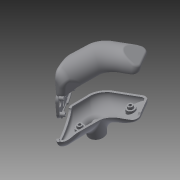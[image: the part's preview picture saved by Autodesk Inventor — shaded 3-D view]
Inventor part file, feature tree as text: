
AUTODESK INVENTOR PART (.ipt)
format: ipt  version: 2014 SP1 (Build 180222100, 222)  size: 21,332,480 bytes
history: native  units: in
note: dims shown in document units (in); Inventor stores cm internally (conversion verified against a paired STEP export)
features: sketch x38, surface_op x32, other x30, extrude x28, fillet x22, draft x19, chamfer x18, plane x14, projected_geometry x6, shell x4, move_body x3, loft x2, delete_face x1, boolean_combine x1, split x1
ambient origin geometry x8: Origin, YZ Plane, XZ Plane, XY Plane, X Axis, Y Axis, Z Axis, Center Point
bodies: Solid1 (feature_tree), Solid2 (feature_tree), Solid5 (feature_tree), Solid8 (feature_tree), Solid9 (feature_tree), Solid10 (feature_tree), Solid6 (feature_tree), Solid7 (feature_tree)
feature tree (219):
  sketch  "Sketch1"  dims[d0=0.7in d1=0.6in]
  plane  "Work Plane1"
  sketch  "Sketch2"  dims[d2=2.0in d3=0.73in]
  loft  "Loft1"
  plane  "Work Plane3"
  plane  "Work Plane4"
  plane  "Work Plane6"
  delete_face  "Delete Face1"
  surface_op  "Extend1"
  sketch  "Sketch6"  dims[d4=0.68in d5=120.0deg d6=0.8125in d9=0.75in]
  surface_op  "Stitch Surface1"
  extrude  "Extrusion5"  Depth=2.0in
  extrude  "Extrusion6"  Depth=0.8125in TaperAngle=120.0deg
  boolean_combine  "Combine1"
  extrude  "Extrusion7"  TaperAngle=0.0deg  [1 undecoded]
  loft  "Loft5"
  fillet  "Fillet6"  Radius=1.0in
  fillet  "Fillet7"  Radius=0.1969in
  plane  "Work Plane7"
  plane  "Work Plane8"
  extrude  "Extrusion10"  Depth=0.1969in
  draft  "FaceDraft1"
  fillet  "Fillet15"  [1 undecoded]
  extrude  "Extrusion15"  TaperAngle=90.0deg  [1 undecoded]
  fillet  "Fillet19"  Radius=0.35in
  fillet  "Fillet20"  [1 undecoded]
  extrude  "Extrusion9"  Depth=0.1in
  fillet  "Fillet11"  Radius=0.0687in
  fillet  "Fillet22"  Radius=0.75in
  shell  "Shell1"  Thickness=0.875in
  extrude  "Extrusion16"  Depth=0.3937in
  extrude  "Extrusion11"  Depth=0.141in
  draft  "FaceDraft5"
  sketch  "3D Sketch2"
  plane  "Work Plane9"
  extrude  "Extrusion17"  Depth=0.3125in TaperAngle=0.0deg
  plane  "Work Plane10"
  extrude  "Extrusion18"  Depth=0.0172in
  plane  "Work Plane11"
  extrude  "Extrusion19"  Depth=0.225in
  plane  "Work Plane12"
  extrude  "Extrusion20"  Depth=0.13in
  draft  "FaceDraft2"
  draft  "FaceDraft3"
  extrude  "Extrusion21"  Depth=0.4in
  extrude  "Extrusion22"  [1 undecoded]
  sketch  "Sketch25"  dims[d130=-0.625in d131=0.4in]
  extrude  "Extrusion23"  Depth=1.0in TaperAngle=0.0deg
  extrude  "Extrusion24"  Depth=0.28in
  extrude  "Extrusion25"  [1 undecoded]
  draft  "FaceDraft4"
  extrude  "Extrusion26"  Depth=1.0in TaperAngle=0.0deg
  plane  "Work Plane13"
  sketch  "Sketch29"  dims[d140=1.0in d141=0.0in d142=-0.06in]
  plane  "Work Plane14"
  sketch  "Sketch30"  dims[d143=0.28in d144=1.0in d145=0.0in]
  surface_op  "Stitch Surface5"
  surface_op  "Extend3"
  surface_op  "Extend4"
  surface_op  "Stitch Surface6"
  sketch  "Sketch35"  dims[d151=0.13in d152=1.0in d153=0.0in]
  surface_op  "Stitch Surface7"
  split  "Split2"
  sketch  "Sketch39"  dims[d160=0.06in d161=1.0in d162=0.0in]
  extrude  "Extrusion27"  Depth=0.0206in
  chamfer  "Chamfer4"  Distance=1.0in
  chamfer  "Chamfer5"  Distance=1.0in
  chamfer  "Chamfer6"  Distance=1.0in
  chamfer  "Chamfer7"  Distance=1.0in
  chamfer  "Chamfer9"  Distance=1.0in
  chamfer  "Chamfer10"  Distance=1.0in
  chamfer  "Chamfer11"  [1 undecoded]
  chamfer  "Chamfer12"  [1 undecoded]
  chamfer  "Chamfer16"  Distance=0.1969in
  chamfer  "Chamfer17"  [1 undecoded]
  chamfer  "Chamfer18"  Distance=0.1969in
  chamfer  "Chamfer19"  [1 undecoded]
  chamfer  "Chamfer20"  [1 undecoded]
  chamfer  "Chamfer21"  [1 undecoded]
  chamfer  "Chamfer22"  [1 undecoded]
  chamfer  "Chamfer23"  [1 undecoded]
  chamfer  "Chamfer24"  [1 undecoded]
  chamfer  "Chamfer25"  [1 undecoded]
  extrude  "Extrusion29"  TaperAngle=0.0deg  [1 undecoded]
  draft  "FaceDraft6"
  fillet  "Fillet26"  [1 undecoded]
  move_body  "Move Body2"
  move_body  "Move Body3"
  draft  "FaceDraft7"
  draft  "FaceDraft8"
  draft  "FaceDraft9"
  draft  "FaceDraft10"
  extrude  "Extrusion30"  TaperAngle=0.0deg  [1 undecoded]
  draft  "FaceDraft16"
  draft  "FaceDraft17"
  extrude  "Extrusion31"  Depth=0.1969in
  extrude  "Extrusion32"  TaperAngle=0.0deg  [1 undecoded]
  extrude  "Extrusion33"  Depth=0.02in
  draft  "FaceDraft18"
  draft  "FaceDraft19"
  draft  "FaceDraft20"
  fillet  "Fillet28"  Radius=0.02in
  extrude  "Extrusion34"  TaperAngle=0.0deg  [1 undecoded]
  extrude  "Extrusion35"  Depth=0.1969in TaperAngle=0.0deg
  extrude  "Extrusion36"  TaperAngle=0.0deg  [1 undecoded]
  draft  "FaceDraft21"
  draft  "FaceDraft22"
  draft  "FaceDraft23"
  shell  "Shell2"  Thickness=0.1969in
  shell  "Shell3"  Thickness=0.1969in
  shell  "Shell4"  Thickness=0.0in
  fillet  "Fillet32"  Radius=0.1969in
  fillet  "Fillet29"  Radius=0.5in
  fillet  "Fillet30"  Radius=0.35in
  fillet  "Fillet31"  Radius=0.125in
  fillet  "Fillet33"  Radius=0.05in
  extrude  "Extrusion40"  Depth=0.05in TaperAngle=0.0deg
  draft  "FaceDraft26"
  fillet  "Fillet44"  Radius=0.05in
  fillet  "Fillet39"  Radius=0.05in
  move_body  "Move Body4"
  fillet  "Fillet45"  Radius=0.05in
  fillet  "Fillet46"  Radius=0.05in
  fillet  "Fillet37"  Radius=0.05in
  fillet  "Fillet48"  Radius=0.05in
  fillet  "Fillet49"  Radius=0.05in
  fillet  "Fillet50"  Radius=0.05in
  sketch  "Sketch57"  dims[d172=0.0in]
  sketch  "Sketch60"  dims[d173=0.1969in d174=0.0in d175=0.0in d176=0.1969in d177=0.0in d178=0.1969in d179=0.0in d184=0.0in d185=0.0in d187=0.0in d191=0.0in d192=0.0in d193=0.0in d197=0.0in d201=0.0in d204=0.0in d208=0.0in d209=0.1969in d210=0.0in d212=0.02in d213=0.02in d214=0.0in d216=0.1969in d217=0.1969in d218=0.0in d219=0.0in d220=0.1969in d221=0.1969in d222=0.0in d223=0.1969in d227=0.5in d228=0.35in d229=0.125in d233=0.05in d234=0.05in d235=0.0in d236=0.05in d237=0.125in d238=0.1374in d239=0.05in d240=0.125in d241=0.1374in d242=0.05in d243=0.125in d244=0.1374in d245=0.05in d246=0.125in d247=0.1374in d251=0.05in d252=0.125in d253=0.0687in d254=0.05in d255=0.125in d256=0.0687in d257=0.05in d258=0.125in d259=0.0687in d260=0.05in d261=0.125in d262=0.0687in d272=0.05in d273=0.125in d274=0.0687in d275=0.05in d276=0.125in d277=0.0687in d278=0.05in d279=0.125in d280=0.0687in d281=0.05in d282=0.125in d283=0.0687in d284=0.05in d285=0.125in d286=0.0687in d287=0.05in d288=0.125in d289=0.0687in d290=0.05in d291=0.125in d292=0.0687in d293=0.05in d294=0.125in d295=0.0687in d296=0.05in d297=0.125in d298=0.0687in d299=0.0508in d300=0.125in d301=0.0687in d302=0.05in d308=0.05in d309=0.0in d310=0.1374in d311=0.03in d312=0.0in d313=1.0in d314=0.0in d315=0.0in d316=-1.0in d317=0.0in d318=0.0206in d319=0.0206in d320=0.0206in d321=0.0206in d323=0.2756in d324=0.3in d325=0.025in d326=1.0in d327=0.0in d337=0.0206in d338=0.0206in d340=0.45in d341=0.08in d342=0.4in d344=0.52in d345=0.0962in d346=0.05in d347=0.025in d349=0.09in d350=0.0in d351=0.008in d352=0.09in d353=0.0in d354=0.008in d355=0.09in d356=0.0in d357=0.0206in d358=0.0206in d359=0.0206in d360=0.015in d361=0.01in d362=0.01in d363=0.01in d365=0.025in d366=0.04in d367=0.0in d371=0.04in d372=0.0in d373=0.04in d374=0.04in d375=0.0in d376=0.01in d377=0.04in d378=0.008in d379=0.04in d380=0.025in d381=0.0206in d382=0.0206in d383=0.0206in d384=0.04in d385=0.04in d386=0.01in d399=0.05in d400=0.075in d401=0.221in d402=0.0in d403=0.05in d404=0.075in d405=0.488in d406=0.04in d407=0.38in d409=-0.5in d410=0.0in d411=0.0in d412=0.01in d431=0.02in d437=0.01in d438=0.005in d439=0.005in d441=0.004in d442=0.003in d443=0.003in d444=0.2909in d445=0.0033in d446=0.6025in d447=0.1425in d448=0.1769in d449=0.5879in d450=1.0588in d451=0.0385in d452=0.2953in d453=1.2533in d454=1.2286in d455=0.3856in d456=0.075in d457=0.0069in d458=0.0143in]
  plane  "Work Plane2"
  plane  "Work Plane5"
  other  "Srf1"
  other  "Srf2"
  sketch  "Sketch8"  dims[d10=0.0in d11=90.0deg d12=0.0in d13=90.0deg]
  sketch  "Sketch9"  dims[d14=150.0deg d15=-0.5in d45=1.0in d46=0.0in d47=1.0in d48=0.0in d49=0.1969in]
  sketch  "Sketch11"  dims[d50=0.0in d51=0.1969in d52=0.0in]
  sketch  "Sketch12"  dims[d53=1.0in d54=0.0in d56=90.0deg d58=90.0deg]
  other  "Edges5"
  other  "Edges6"
  sketch  "Sketch13"  dims[d62=0.0in d63=90.0deg d64=0.0in d65=90.0deg d66=0.2875in d67=0.35in d78=90.0deg]
  sketch  "Sketch17"  dims[d79=1.0in d80=0.0in d81=0.1in d87=0.0687in d88=0.75in d89=0.875in d90=0.0in]
  sketch  "Sketch18"  dims[d92=0.3937in d93=0.3937in]
  projected_geometry  "Projected Loop3"
  other  "Silhouette Curve2"
  sketch  "Sketch19"  dims[d94=0.2625in d95=0.141in]
  sketch  "Sketch20"  dims[d96=0.5in d97=0.3125in d98=0.0in]
  sketch  "Sketch21"  dims[d107=0.1in d114=0.0172in]
  sketch  "Sketch22"  dims[d117=0.121in d118=0.0in]
  sketch  "Sketch23"  dims[d119=0.1in d120=0.1in d121=0.13in d122=0.1969in d123=0.3in d124=0.2169in d125=0.225in]
  sketch  "Sketch24"  dims[d126=0.15in d127=0.0in d129=0.13in]
  sketch  "Sketch26"  dims[d132=1.0in d133=0.0in d134=-0.875in]
  sketch  "Sketch27"  dims[d135=0.4in d136=1.0in d137=0.0in]
  sketch  "Sketch28"  dims[d138=-0.06in d139=0.28in]
  other  "Srf3"
  other  "Srf4"
  other  "Srf5"
  other  "Srf6"
  other  "Srf7"
  other  "Srf8"
  other  "Srf12"
  other  "Srf13"
  other  "Srf15"
  other  "Srf17"
  other  "Srf18"
  other  "Srf19"
  other  "Srf21"
  other  "Srf24"
  other  "Srf25"
  sketch  "Sketch33"  dims[d146=0.0206in d147=0.0206in]
  sketch  "Sketch34"  dims[d148=0.13in d149=1.0in d150=0.0in]
  other  "Srf28"
  other  "Srf30"
  other  "Srf31"
  other  "Srf32"
  other  "Srf33"
  other  "Srf34"
  other  "Srf35"
  sketch  "Sketch36"  dims[d154=0.06in]
  other  "Srf36"
  other  "Srf37"
  other  "Srf38"
  sketch  "Sketch37"  dims[d155=0.06in d156=1.0in d157=0.0in d158=1.0in d159=0.0in]
  sketch  "Sketch41"  dims[d163=0.0206in]
  sketch  "Sketch43"  dims[d164=0.23in d165=1.0in d166=0.0in]
  sketch  "Sketch44"  dims[d167=15.0deg]
  sketch  "Sketch45"  dims[d168=0.125in]
  sketch  "Sketch46"  dims[d169=0.125in]
  sketch  "Sketch47"  dims[d170=0.0in]
  projected_geometry  "Projected Loop4"
  projected_geometry  "Projected Loop5"
  sketch  "Sketch51"  dims[d171=0.1969in]
  projected_geometry  "Projected Loop13"
  surface_op  "Boundary Patch1"
  surface_op  "Boundary Patch2"
  projected_geometry  "Project Cut Edges1"
  projected_geometry  "Project Cut Edges2"
  surface_op  "Boundary Patch3"
  surface_op  "Boundary Patch4"
  surface_op  "Boundary Patch5"
  surface_op  "Boundary Patch6"
  surface_op  "Boundary Patch7"
  surface_op  "Boundary Patch8"
  surface_op  "Boundary Patch12"
  surface_op  "Boundary Patch13"
  surface_op  "Boundary Patch15"
  surface_op  "Boundary Patch17"
  surface_op  "Boundary Patch18"
  surface_op  "Boundary Patch19"
  surface_op  "Boundary Patch21"
  surface_op  "Boundary Patch23"
  surface_op  "Boundary Patch24"
  surface_op  "Boundary Patch26"
  surface_op  "Boundary Patch27"
  surface_op  "Boundary Patch28"
  surface_op  "Boundary Patch29"
  surface_op  "Boundary Patch30"
  surface_op  "Boundary Patch31"
  surface_op  "Boundary Patch32"
  surface_op  "Boundary Patch33"
note: 22 required parameter values undecoded (feature->parameter linkage not recoverable at this tier; creation-order binding heuristic only, values carry confidence <= 0.55)
